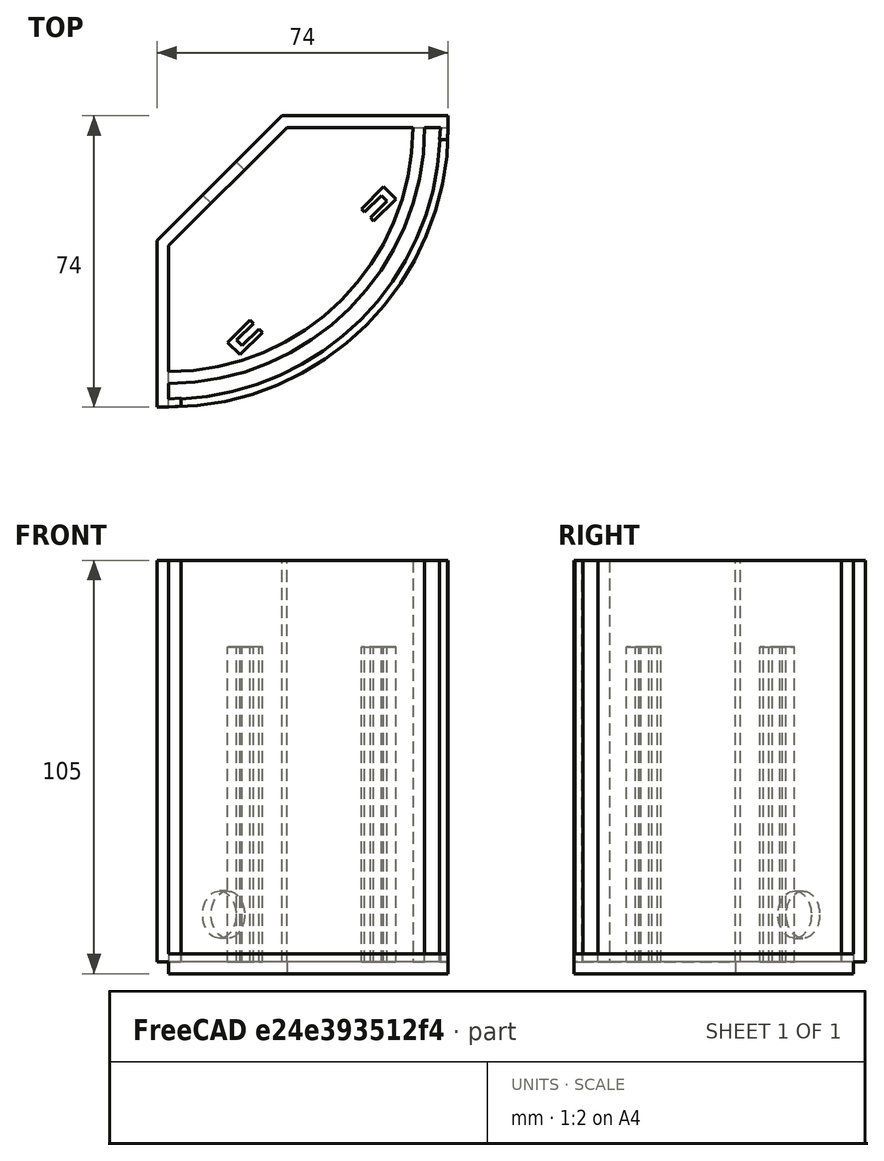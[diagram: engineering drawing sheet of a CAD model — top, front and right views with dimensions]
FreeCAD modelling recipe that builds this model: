
FCSTD DOCUMENT  (FreeCAD 0.19R24276 (Git))
Label: PhotoHolder
License: All rights reserved
LicenseURL: http://en.wikipedia.org/wiki/All_rights_reserved
objects: Sketcher::SketchObject×7, PartDesign::Pad×5, PartDesign::Pocket×2, PartDesign::Revolution×1, PartDesign::Body×1
note: 24 computed .brp shape members not serialized (recipe doc carries the construction recipe); baked Part::Feature solids carry a one-line shape summary decoded from their .brp

FEATURE [Sketcher::SketchObject] Sketch
  FullyConstrained = true
  MapMode = 5
  Placement = pos=(0,0,0) rot=(1,0,0;1.5708rad)
  Support = -> [XZ_Plane]
  sketch-geometry (10):
    g0: LineSegment StartX=0 StartY=0 StartZ=0 EndX=71 EndY=0 EndZ=0
    g1: LineSegment StartX=71 StartY=0 StartZ=0 EndX=71 EndY=5 EndZ=0
    g2: LineSegment StartX=71 StartY=5 StartZ=0 EndX=69 EndY=5 EndZ=0
    g3: LineSegment StartX=69 StartY=5 StartZ=0 EndX=69 EndY=3 EndZ=0
    g4: LineSegment StartX=69 StartY=3 StartZ=0 EndX=65 EndY=3 EndZ=0
    g5: LineSegment StartX=65 StartY=3 StartZ=0 EndX=65 EndY=105 EndZ=0
    g6: LineSegment StartX=65 StartY=105 StartZ=0 EndX=62 EndY=105 EndZ=0
    g7: LineSegment StartX=62 StartY=105 StartZ=0 EndX=62 EndY=3 EndZ=0
    g8: LineSegment StartX=62 StartY=3 StartZ=0 EndX=0 EndY=3 EndZ=0
    g9: LineSegment StartX=0 StartY=3 StartZ=0 EndX=0 EndY=0 EndZ=0
  constraints (29):
    c: Horizontal(g0)
    c: Coincident(g0,g1)
    c: Vertical(g1)
    c: Coincident(g1,g2)
    c: Coincident(g2,g3)
    c: Vertical(g3)
    c: Coincident(g3,g4)
    c: Horizontal(g4)
    c: Coincident(g4,g5)
    c: Vertical(g5)
    c: Coincident(g5,g6)
    c: Coincident(g6,g7)
    c: Vertical(g7)
    c: Coincident(g7,g8)
    c: Horizontal(g8)
    c: Coincident(g8,g9)
    c: Coincident(g9,g0)
    c: Vertical(g9)
    c: Coincident(g0,g-1)
    c: DistanceX(g0,g4) = 65
    c: Horizontal(g6)
    c: Horizontal(g2)
    c: Distance(g6) = 3
    c: Distance(g4) = 4
    c: Distance(g2) = 2
    c: Distance(g9) = 3
    c: Distance(g1) = 5
    c: Distance(g7) = 102
    c: Distance(g5) = 102
FEATURE [PartDesign::Revolution] Revolution
  Angle = 90
  Axis = (0,2e-16,1)
  Base = (0,0,0)
  Placement = pos=(0,0,0) rot=(1,0,0;1.5708rad)
  Profile = -> Sketch
  ReferenceAxis = -> Sketch [V_Axis]
  Reversed = true
FEATURE [Sketcher::SketchObject] Sketch001
  FullyConstrained = true
  MapMode = 5
  Placement = pos=(0,2e-15,3) rot=(0,0,1;3.14159rad)
  Support = -> [Revolution]
  sketch-geometry (3):
    g0: LineSegment StartX=0 StartY=0 StartZ=0 EndX=-30 EndY=0 EndZ=0
    g1: LineSegment StartX=-30 StartY=0 StartZ=0 EndX=0 EndY=30 EndZ=0
    g2: LineSegment StartX=0 StartY=30 StartZ=0 EndX=0 EndY=0 EndZ=0
  constraints (8):
    c: Coincident(g-1,g0)
    c: PointOnObject(g0,g-1)
    c: Coincident(g0,g1)
    c: PointOnObject(g1,g-2)
    c: Coincident(g1,g2)
    c: Coincident(g2,g0)
    c: Distance(g2) = 30
    c: Distance(g0) = 30
FEATURE [PartDesign::Pocket] Pocket
  BaseFeature = -> Revolution
  Length = 3
  Length2 = 100
  Placement = pos=(0,0,0) rot=(1,0,0;1.5708rad)
  Profile = -> Sketch001
  Type = 0
FEATURE [Sketcher::SketchObject] Sketch002
  FullyConstrained = true
  MapMode = 5
  Placement = pos=(0,3.3e-15,3) rot=(0,0,1;3.14159rad)
  Support = -> [Pocket]
  sketch-geometry (8):
    g0: LineSegment StartX=0 StartY=71 StartZ=0 EndX=0 EndY=30 EndZ=0
    g1: LineSegment StartX=0 StartY=30 StartZ=0 EndX=-30 EndY=1.78e-14 EndZ=0
    g2: LineSegment StartX=-30 StartY=1.78e-14 StartZ=0 EndX=-71 EndY=1.78e-14 EndZ=0
    g3: LineSegment StartX=-71 StartY=1.78e-14 StartZ=0 EndX=-71 EndY=-3 EndZ=0
    g4: LineSegment StartX=-71 StartY=-3 StartZ=0 EndX=-28.7574 EndY=-3 EndZ=0
    g5: LineSegment StartX=-28.7574 StartY=-3 StartZ=0 EndX=3 EndY=28.7574 EndZ=0
    g6: LineSegment StartX=3 StartY=28.7574 StartZ=0 EndX=3 EndY=71 EndZ=0
    g7: LineSegment StartX=3 StartY=71 StartZ=0 EndX=0 EndY=71 EndZ=0
  constraints (24):
    c: Vertical(g0)
    c: Coincident(g0,g1)
    c: Coincident(g1,g2)
    c: Horizontal(g2)
    c: Coincident(g2,g3)
    c: Coincident(g3,g4)
    c: Horizontal(g4)
    c: Coincident(g4,g5)
    c: Coincident(g5,g6)
    c: Coincident(g6,g7)
    c: Coincident(g7,g0)
    c: Horizontal(g7)
    c: Vertical(g6)
    c: Vertical(g3)
    c: Distance(g0) = 41
    c: Distance(g7) = 3
    c: Distance(g2) = 41
    c: Distance(g3) = 3
    c: Angle(g0,g1) = 2.35619
    c: Angle(g6,g5) = 2.35619
    c: DistanceX(g1,g-1) = 30
    c: DistanceY(g-1,g0) = 30
    c: DistanceX(g-1,g5) = 3
    c: DistanceY(g5,g0) = 1.2426
FEATURE [PartDesign::Pad] Pad
  BaseFeature = -> Pocket
  Direction = (1,1,1)
  Length = 102
  Length2 = 100
  Placement = pos=(0,0,0) rot=(1,0,0;1.5708rad)
  Profile = -> Sketch002
  Type = 0
FEATURE [Sketcher::SketchObject] Sketch003
  FullyConstrained = true
  MapMode = 5
  Placement = pos=(0,4.7e-15,3) rot=(0,0,1;3.14159rad)
  Support = -> [Pad]
  sketch-geometry (4):
    g0: LineSegment StartX=0 StartY=71 StartZ=0 EndX=0 EndY=69 EndZ=0
    g1: LineSegment StartX=0 StartY=69 StartZ=0 EndX=-3.09082 EndY=68.7616 EndZ=0
    g2: LineSegment StartX=-3.09082 StartY=68.7616 StartZ=0 EndX=-3.09082 EndY=70.7616 EndZ=0
    g3: LineSegment StartX=-3.09082 StartY=70.7616 StartZ=0 EndX=0 EndY=71 EndZ=0
  constraints (12):
    c: Vertical(g0)
    c: Coincident(g0,g1)
    c: Coincident(g1,g2)
    c: Vertical(g2)
    c: Coincident(g2,g3)
    c: Coincident(g3,g0)
    c: Distance(g0) = 2
    c: Distance(g2) = 2
    c: Distance(g3) = 3.1
    c: Angle(g0,g1) = 1.64777
    c: DistanceY(g-1,g0) = 71
    c: DistanceX(g-1,g0) = 0
FEATURE [PartDesign::Pad] Pad001
  BaseFeature = -> Pad
  Direction = (1,1,1)
  Length = 102
  Length2 = 100
  Placement = pos=(0,0,0) rot=(1,0,0;1.5708rad)
  Profile = -> Sketch003
  Type = 0
FEATURE [Sketcher::SketchObject] Sketch004
  FullyConstrained = true
  MapMode = 5
  Placement = pos=(0,6e-15,3) rot=(0,0,1;3.14159rad)
  Support = -> [Pad001]
  sketch-geometry (4):
    g0: LineSegment StartX=-71 StartY=0 StartZ=0 EndX=-69 EndY=0 EndZ=0
    g1: LineSegment StartX=-69 StartY=0 StartZ=0 EndX=-68.7616 EndY=3.09082 EndZ=0
    g2: LineSegment StartX=-68.7616 StartY=3.09082 StartZ=0 EndX=-70.7616 EndY=3.09082 EndZ=0
    g3: LineSegment StartX=-70.7616 StartY=3.09082 StartZ=0 EndX=-71 EndY=0 EndZ=0
  constraints (12):
    c: Horizontal(g0)
    c: Coincident(g0,g1)
    c: Coincident(g1,g2)
    c: Coincident(g2,g3)
    c: Coincident(g3,g0)
    c: Distance(g0) = 2
    c: Distance(g2) = 2
    c: Distance(g1) = 3.1
    c: Distance(g3) = 3.1
    c: Angle(g1,g0) = 1.64777
    c: DistanceY(g-1,g0) = 0
    c: DistanceX(g0,g-1) = 71
FEATURE [PartDesign::Pad] Pad002
  BaseFeature = -> Pad001
  Direction = (1,1,1)
  Length = 102
  Length2 = 100
  Placement = pos=(0,0,0) rot=(1,0,0;1.5708rad)
  Profile = -> Sketch004
  Type = 0
FEATURE [Sketcher::SketchObject] Sketch005
  FullyConstrained = true
  MapMode = 5
  Placement = pos=(12.8787,-12.8787,3.15e-14) rot=(-0.862856,-0.357407,0.357407;1.71777rad)
  Support = -> [Pad002]
  sketch-geometry (1):
    g0: Circle CenterX=0 CenterY=-15 CenterZ=0 NormalX=0 NormalY=0 NormalZ=1 AngleXU=0 Radius=6
  constraints (3):
    c: Radius(g0) = 6
    c: DistanceX(g-1,g0) = 0
    c: DistanceY(g0,g-1) = 15
FEATURE [PartDesign::Pocket] Pocket001
  BaseFeature = -> Pad002
  Length = 3
  Length2 = 100
  Placement = pos=(0,0,0) rot=(1,0,0;1.5708rad)
  Profile = -> Sketch005
  Type = 0
FEATURE [Sketcher::SketchObject] Sketch006
  FullyConstrained = false
  MapMode = 5
  Placement = pos=(0,8.7e-15,3) rot=(0,0,1;3.14159rad)
  Support = -> [Pocket001]
  sketch-geometry (16):
    g0: LineSegment StartX=-23.7702 StartY=52.0524 StartZ=0 EndX=-18.1113 EndY=57.7072 EndZ=0
    g1: LineSegment StartX=-18.1113 StartY=57.7072 StartZ=0 EndX=-15.0011 EndY=54.5948 EndZ=0
    g2: LineSegment StartX=-15.0011 StartY=54.5948 StartZ=0 EndX=-20.66 EndY=48.94 EndZ=0
    g3: LineSegment StartX=-20.66 StartY=48.94 StartZ=0 EndX=-21.5082 EndY=49.7888 EndZ=0
    g4: LineSegment StartX=-21.5082 StartY=49.7888 StartZ=0 EndX=-17.2641 EndY=54.03 EndZ=0
    g5: LineSegment StartX=-17.2641 StartY=54.03 StartZ=0 EndX=-18.6778 EndY=55.4447 EndZ=0
    g6: LineSegment StartX=-18.6778 StartY=55.4447 StartZ=0 EndX=-22.9219 EndY=51.2036 EndZ=0
    g7: LineSegment StartX=-22.9219 StartY=51.2036 StartZ=0 EndX=-23.7702 EndY=52.0524 EndZ=0
    g8: LineSegment StartX=-57.7111 StartY=18.1115 StartZ=0 EndX=-52.0539 EndY=23.768 EndZ=0
    g9: LineSegment StartX=-52.0539 StartY=23.768 StartZ=0 EndX=-51.2054 EndY=22.9194 EndZ=0
    g10: LineSegment StartX=-51.2054 StartY=22.9194 StartZ=0 EndX=-55.4483 EndY=18.677 EndZ=0
    g11: LineSegment StartX=-55.4483 StartY=18.677 StartZ=0 EndX=-54.0342 EndY=17.2627 EndZ=0
    g12: LineSegment StartX=-54.0342 StartY=17.2627 StartZ=0 EndX=-49.7913 EndY=21.5051 EndZ=0
    g13: LineSegment StartX=-49.7913 StartY=21.5051 StartZ=0 EndX=-48.9428 EndY=20.6565 EndZ=0
    g14: LineSegment StartX=-48.9428 StartY=20.6565 StartZ=0 EndX=-54.6 EndY=15 EndZ=0
    g15: LineSegment StartX=-54.6 StartY=15 StartZ=0 EndX=-57.7111 EndY=18.1115 EndZ=0
  constraints (46):
    c: Coincident(g0,g1)
    c: Coincident(g1,g2)
    c: Coincident(g2,g3)
    c: Coincident(g3,g4)
    c: Coincident(g4,g5)
    c: Coincident(g5,g6)
    c: Coincident(g6,g7)
    c: Coincident(g7,g0)
    c: Coincident(g8,g9)
    c: Coincident(g9,g10)
    c: Coincident(g10,g11)
    c: Coincident(g11,g12)
    c: Coincident(g12,g13)
    c: Coincident(g13,g14)
    c: Coincident(g14,g15)
    c: Coincident(g15,g8)
    c: Angle(g1,g2) = 1.5708
    c: Angle(g0,g1) = 1.5708
    c: Angle(g6,g5) = 1.5708
    c: Angle(g5,g4) = 1.5708
    c: Angle(g6,g7) = 1.5708
    c: Angle(g7,g0) = 1.5708
    c: Angle(g3,g4) = 1.5708
    c: Distance(g5) = 2
    c: Distance(g3) = 1.2
    c: Distance(g7) = 1.2
    c: Distance(g6) = 6
    c: Distance(g4) = 6
    c: Distance(g0) = 8
    c: Angle(g13,g14) = 1.5708
    c: Angle(g14,g15) = 1.5708
    c: Angle(g15,g8) = 1.5708
    c: Angle(g8,g9) = 1.5708
    c: Angle(g9,g10) = 1.5708
    c: Angle(g11,g10) = 1.5708
    c: Angle(g12,g11) = 1.5708
    c: Distance(g11) = 2
    c: Distance(g9) = 1.2
    c: Distance(g13) = 1.2
    c: Distance(g10) = 6
    c: Distance(g12) = 6
    c: Distance(g14) = 8
    c: DistanceY(g-1,g14) = 15
    c: DistanceX(g14,g-1) = 54.6
    c: DistanceY(g-1,g2) = 48.94
    c: DistanceX(g2,g-1) = 20.66
FEATURE [PartDesign::Pad] Pad003
  BaseFeature = -> Pocket001
  Direction = (1,1,1)
  Length = 80
  Length2 = 100
  Placement = pos=(0,0,0) rot=(1,0,0;1.5708rad)
  Profile = -> Sketch006
  Type = 0
FEATURE [PartDesign::Pad] Pad004
  BaseFeature = -> Pad003
  Direction = (1,1,1)
  Length = 80
  Length2 = 100
  Placement = pos=(0,0,0) rot=(1,0,0;1.5708rad)
  Profile = -> Sketch006
  Type = 0
FEATURE [PartDesign::Body] Body
  Group = -> [Sketch,Revolution,Sketch001,Pocket,Sketch002,Pad,Sketch003,Pad001,Sketch004,Pad002,Sketch005,Pocket001,Sketch006,Pad003,Pad004]
  Origin = -> Origin
  Tip = -> Pad004
